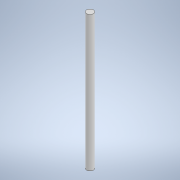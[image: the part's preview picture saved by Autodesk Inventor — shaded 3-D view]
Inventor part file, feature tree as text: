
AUTODESK INVENTOR PART (.ipt)
format: ipt  version: 2020 (Build 240168000, 168)  size: 90,112 bytes
history: native  units: mm
features: extrude x1, sketch x1
ambient origin geometry x8: Origin, YZ Plane, XZ Plane, XY Plane, X Axis, Y Axis, Z Axis, Center Point
bodies: Solid1 (feature_tree)
feature tree (2):
  extrude  "Extrusion1"  Depth=30.0mm TaperAngle=0.0deg
  sketch  "Sketch1"  dims[d0=1.5mm d1=30.0mm d2=0.0mm]
